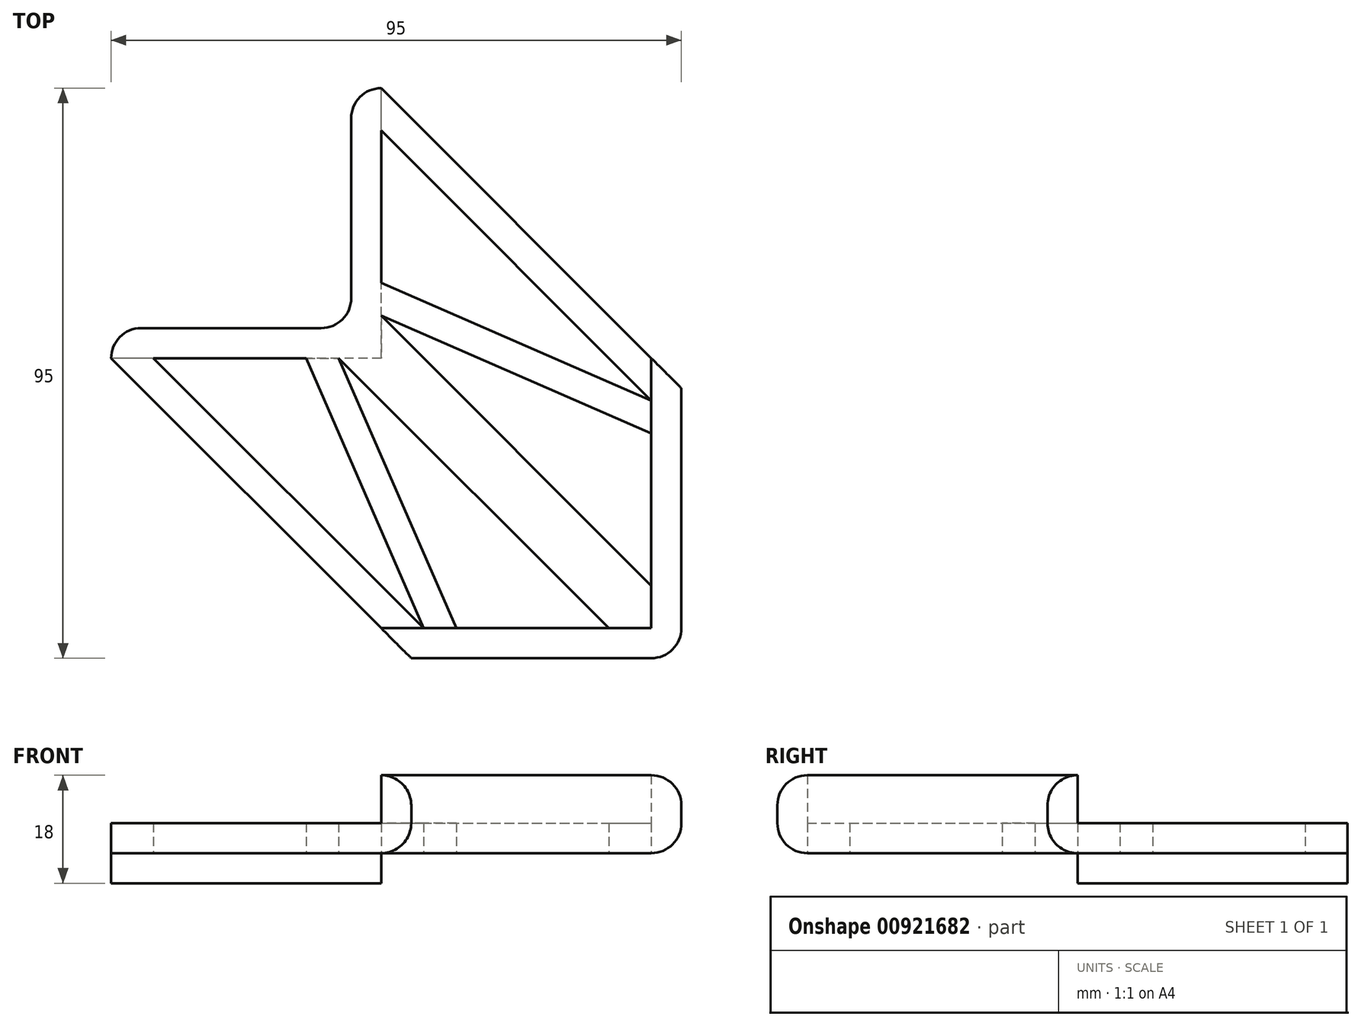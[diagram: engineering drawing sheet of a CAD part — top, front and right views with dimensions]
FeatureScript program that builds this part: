
annotation { "Feature Type Name" : "Feature", "Feature Type Description" : "" }
export const myFeature = defineFeature(function(context is Context, id is Id, definition is map)
    precondition{}
    {
        {
            var Q0;
            Q0=qCreatedBy(makeId("Top.planeOp"),FACE);
            var sketch = newSketch(context, id + "F0", { "sketchPlane" : qUnion([Q0])});
            skLineSegment(sketch, "E0", {"start": v(-5, 45) * mm, "end": v(-5, 5) * mm});
            skLineSegment(sketch, "E1", {"start": v(-5, 5) * mm, "end": v(-45, 5) * mm});
            skLineSegment(sketch, "E2", {"start": v(-45, 5) * mm, "end": v(-45, 0) * mm});
            skLineSegment(sketch, "E3", {"start": v(-45, 0) * mm, "end": v(0, -45) * mm});
            skLineSegment(sketch, "E4", {"start": v(0, -45) * mm, "end": v(0, -50) * mm});
            skLineSegment(sketch, "E5", {"start": v(0, -50) * mm, "end": v(50, -50) * mm});
            skLineSegment(sketch, "E6", {"start": v(50, -50) * mm, "end": v(50, 0) * mm});
            skLineSegment(sketch, "E7", {"start": v(50, 0) * mm, "end": v(45, 0) * mm});
            skLineSegment(sketch, "E8", {"start": v(45, 0) * mm, "end": v(0, 45) * mm});
            skLineSegment(sketch, "E9", {"start": v(0, 45) * mm, "end": v(-5, 45) * mm});
            skLineSegment(sketch, "E10.0", {"start": v(45, -45) * mm, "end": v(45, -7.07) * mm});
            skLineSegment(sketch, "E10.1", {"start": v(0, 37.93) * mm, "end": v(0, 0) * mm});
            skLineSegment(sketch, "E10.2", {"start": v(0, 0) * mm, "end": v(-37.93, 0) * mm});
            skLineSegment(sketch, "E10.3", {"start": v(45, -7.07) * mm, "end": v(0, 37.93) * mm});
            skLineSegment(sketch, "E10.4", {"start": v(-37.93, 0) * mm, "end": v(7.07, -45) * mm});
            skLineSegment(sketch, "E10.5", {"start": v(7.07, -45) * mm, "end": v(45, -45) * mm});
            skSolve(sketch);
        }
        {
            var Q0;
            Q0 = qSketchRegion(id + "F0", true);
            extrude(context, id + "F1", {"entities" : qUnion([Q0]), "depth" : 5 * mm, "offsetDistance" : 25 * mm});
        }
        {
            var Q0;
            Q0=makeQuery(id+"F1.opExtrude","CAP_FACE",FACE,{"disambiguationData":[OSD([sQuery(id+"F0.wireOp",EDGE,"E0"),sQuery(id+"F0.wireOp",EDGE,"E1"),sQuery(id+"F0.wireOp",EDGE,"E2"),sQuery(id+"F0.wireOp",EDGE,"E3"),sQuery(id+"F0.wireOp",EDGE,"E4"),sQuery(id+"F0.wireOp",EDGE,"E5"),sQuery(id+"F0.wireOp",EDGE,"E6"),sQuery(id+"F0.wireOp",EDGE,"E7"),sQuery(id+"F0.wireOp",EDGE,"E8"),sQuery(id+"F0.wireOp",EDGE,"E9")])],"isStart":true});
            var sketch = newSketch(context, id + "F2", { "sketchPlane" : qUnion([Q0])});
            skLineSegment(sketch, "E11", {"start": v(0, 0) * mm, "end": v(0, -45) * mm});
            skLineSegment(sketch, "E12", {"start": v(0, -45) * mm, "end": v(-5, -45) * mm});
            skLineSegment(sketch, "E13", {"start": v(-5, -45) * mm, "end": v(-5, -5) * mm});
            skLineSegment(sketch, "E14", {"start": v(-5, -5) * mm, "end": v(-45, -5) * mm});
            skLineSegment(sketch, "E15", {"start": v(-45, -5) * mm, "end": v(-45, 0) * mm});
            skLineSegment(sketch, "E16", {"start": v(-45, 0) * mm, "end": v(0, 0) * mm});
            skSolve(sketch);
        }
        {
            var Q0;
            Q0 = qSketchRegion(id + "F2", true);
            extrude(context, id + "F3", {"entities" : qUnion([Q0]), "operationType" : NewBodyOperationType.ADD, "depth" : 5 * mm, "offsetDistance" : 25 * mm});
        }
        {
            var Q0;
            Q0=makeQuery(id+"F1.opExtrude","CAP_FACE",FACE,{"disambiguationData":[OSD([sQuery(id+"F0.wireOp",EDGE,"E0"),sQuery(id+"F0.wireOp",EDGE,"E1"),sQuery(id+"F0.wireOp",EDGE,"E2"),sQuery(id+"F0.wireOp",EDGE,"E3"),sQuery(id+"F0.wireOp",EDGE,"E4"),sQuery(id+"F0.wireOp",EDGE,"E5"),sQuery(id+"F0.wireOp",EDGE,"E6"),sQuery(id+"F0.wireOp",EDGE,"E7"),sQuery(id+"F0.wireOp",EDGE,"E8"),sQuery(id+"F0.wireOp",EDGE,"E9")])],"isStart":false});
            var sketch = newSketch(context, id + "F4", { "sketchPlane" : qUnion([Q0])});
            skLineSegment(sketch, "E17", {"start": v(45, 0) * mm, "end": v(50, 0) * mm});
            skLineSegment(sketch, "E18", {"start": v(50, 0) * mm, "end": v(50, -50) * mm});
            skLineSegment(sketch, "E19", {"start": v(50, -50) * mm, "end": v(0, -50) * mm});
            skLineSegment(sketch, "E20", {"start": v(0, -50) * mm, "end": v(0, -45) * mm});
            skLineSegment(sketch, "E21", {"start": v(0, -45) * mm, "end": v(45, -45) * mm});
            skLineSegment(sketch, "E22", {"start": v(45, -45) * mm, "end": v(45, 0) * mm});
            skSolve(sketch);
        }
        {
            var Q0;
            Q0 = qSketchRegion(id + "F4", true);
            extrude(context, id + "F5", {"entities" : qUnion([Q0]), "operationType" : NewBodyOperationType.ADD, "depth" : 8 * mm, "offsetDistance" : 25 * mm});
        }
        {
            var Q0;
            Q0=makeQuery(id+"F5.boolean.opBoolean","MERGE",EDGE,{"derivedFrom":[makeQuery(id+"F1.opExtrude","SWEPT_EDGE",EDGE,{"disambiguationData":[OSD([sQuery(id+"F0.wireOp",EDGE,"E4"),sQuery(id+"F0.wireOp",EDGE,"E5")])]}),makeQuery(id+"F5.opExtrude","SWEPT_EDGE",EDGE,{"disambiguationData":[OSD([sQuery(id+"F4.wireOp",EDGE,"E19"),sQuery(id+"F4.wireOp",EDGE,"E20")])]})]});
            var Q1;
            Q1=makeQuery(id+"F5.boolean.opBoolean","MERGE",EDGE,{"derivedFrom":[makeQuery(id+"F1.opExtrude","SWEPT_EDGE",EDGE,{"disambiguationData":[OSD([sQuery(id+"F0.wireOp",EDGE,"E6"),sQuery(id+"F0.wireOp",EDGE,"E7")])]}),makeQuery(id+"F5.opExtrude","SWEPT_EDGE",EDGE,{"disambiguationData":[OSD([sQuery(id+"F4.wireOp",EDGE,"E17"),sQuery(id+"F4.wireOp",EDGE,"E18")])]})]});
            chamfer(context, id + "F6", {"entities" : qUnion([Q0, Q1]), "width" : 5 * mm, "tangentPropagation" : true});
        }
        {
            var Q0;
            Q0=makeQuery(id+"F5.boolean.opBoolean","MERGE",EDGE,{"derivedFrom":[makeQuery(id+"F1.opExtrude","SWEPT_EDGE",EDGE,{"disambiguationData":[OSD([sQuery(id+"F0.wireOp",EDGE,"E5"),sQuery(id+"F0.wireOp",EDGE,"E6")])]}),makeQuery(id+"F5.opExtrude","SWEPT_EDGE",EDGE,{"disambiguationData":[OSD([sQuery(id+"F4.wireOp",EDGE,"E18"),sQuery(id+"F4.wireOp",EDGE,"E19")])]})]});
            var Q1;
            Q1=makeQuery(id+"F3.boolean.opBoolean","MERGE",EDGE,{"derivedFrom":[makeQuery(id+"F1.opExtrude","SWEPT_EDGE",EDGE,{"disambiguationData":[OSD([sQuery(id+"F0.wireOp",EDGE,"E0"),sQuery(id+"F0.wireOp",EDGE,"E9")])]}),makeQuery(id+"F3.opExtrude","SWEPT_EDGE",EDGE,{"disambiguationData":[OSD([sQuery(id+"F2.wireOp",EDGE,"E12"),sQuery(id+"F2.wireOp",EDGE,"E13")])]})]});
            var Q2;
            Q2=makeQuery(id+"F3.boolean.opBoolean","MERGE",EDGE,{"derivedFrom":[makeQuery(id+"F1.opExtrude","SWEPT_EDGE",EDGE,{"disambiguationData":[OSD([sQuery(id+"F0.wireOp",EDGE,"E1"),sQuery(id+"F0.wireOp",EDGE,"E2")])]}),makeQuery(id+"F3.opExtrude","SWEPT_EDGE",EDGE,{"disambiguationData":[OSD([sQuery(id+"F2.wireOp",EDGE,"E14"),sQuery(id+"F2.wireOp",EDGE,"E15")])]})]});
            var Q3;
            Q3=makeQuery(id+"F3.boolean.opBoolean","MERGE",EDGE,{"derivedFrom":[makeQuery(id+"F1.opExtrude","SWEPT_EDGE",EDGE,{"disambiguationData":[OSD([sQuery(id+"F0.wireOp",EDGE,"E0"),sQuery(id+"F0.wireOp",EDGE,"E1")])]}),makeQuery(id+"F3.opExtrude","SWEPT_EDGE",EDGE,{"disambiguationData":[OSD([sQuery(id+"F2.wireOp",EDGE,"E13"),sQuery(id+"F2.wireOp",EDGE,"E14")])]})]});
            var Q4;
            Q4=makeQuery(id+"F5.opExtrude","CAP_EDGE",EDGE,{"disambiguationData":[OSD([sQuery(id+"F4.wireOp",EDGE,"E18")])],"isStart":false});
            var Q5;
            Q5=makeQuery(id+"F5.opExtrude","CAP_EDGE",EDGE,{"disambiguationData":[OSD([sQuery(id+"F4.wireOp",EDGE,"E19")])],"isStart":false});
            var Q6;
            Q6=makeQuery(id+"F1.opExtrude","CAP_EDGE",EDGE,{"disambiguationData":[OSD([sQuery(id+"F0.wireOp",EDGE,"E5")])],"isStart":true});
            var Q7;
            Q7=makeQuery(id+"F1.opExtrude","CAP_EDGE",EDGE,{"disambiguationData":[OSD([sQuery(id+"F0.wireOp",EDGE,"E6")])],"isStart":true});
            fillet(context, id + "F7", {"entities" : qUnion([Q0, Q1, Q2, Q3, Q4, Q5, Q6, Q7]), "radius" : 5 * mm, "tangentPropagation" : true, "allowEdgeOverflow" : false});
        }
        {
            var Q0;
            Q0=qCreatedBy(makeId("Top.planeOp"),FACE);
            var sketch = newSketch(context, id + "F8", { "sketchPlane" : qUnion([Q0])});
            skLineSegment(sketch, "E23", {"start": v(-7.07, 0) * mm, "end": v(37.93, -45) * mm});
            skLineSegment(sketch, "E24", {"start": v(37.93, -45) * mm, "end": v(45, -45) * mm});
            skLineSegment(sketch, "E25", {"start": v(45, -45) * mm, "end": v(45, -37.93) * mm});
            skLineSegment(sketch, "E26", {"start": v(45, -37.93) * mm, "end": v(0, 7.07) * mm});
            skLineSegment(sketch, "E27", {"start": v(0, 7.07) * mm, "end": v(0, 0) * mm});
            skLineSegment(sketch, "E28", {"start": v(0, 0) * mm, "end": v(-7.07, 0) * mm});
            skSolve(sketch);
        }
        {
            var Q0;
            Q0 = qSketchRegion(id + "F8", true);
            extrude(context, id + "F9", {"entities" : qUnion([Q0]), "operationType" : NewBodyOperationType.ADD, "depth" : 5 * mm, "offsetDistance" : 25 * mm});
        }
        {
            var Q0;
            Q0=qCreatedBy(makeId("Top.planeOp"),FACE);
            var Q1;
            Q1=qCreatedBy(makeId("Top.planeOp"),FACE);
            var sketch = newSketch(context, id + "F10", { "sketchPlane" : qUnion([Q0, Q1])});
            skLineSegment(sketch, "E29", {"start": v(0, 12.52) * mm, "end": v(45, -7.07) * mm});
            skLineSegment(sketch, "E30", {"start": v(45, -7.07) * mm, "end": v(45, -12.52) * mm});
            skLineSegment(sketch, "E31", {"start": v(45, -12.52) * mm, "end": v(0, 7.07) * mm});
            skLineSegment(sketch, "E32", {"start": v(0, 7.07) * mm, "end": v(0, 12.52) * mm});
            skLineSegment(sketch, "E33", {"start": v(-7.07, 0) * mm, "end": v(12.52, -45) * mm});
            skLineSegment(sketch, "E34", {"start": v(12.52, -45) * mm, "end": v(7.07, -45) * mm});
            skLineSegment(sketch, "E35", {"start": v(7.07, -45) * mm, "end": v(-12.52, 0) * mm});
            skLineSegment(sketch, "E36", {"start": v(-12.52, 0) * mm, "end": v(-7.07, 0) * mm});
            skSolve(sketch);
        }
        {
            var Q0;
            Q0 = qSketchRegion(id + "F10", true);
            extrude(context, id + "F11", {"entities" : qUnion([Q0]), "operationType" : NewBodyOperationType.ADD, "depth" : 5 * mm, "offsetDistance" : 25 * mm});
        }
    });
